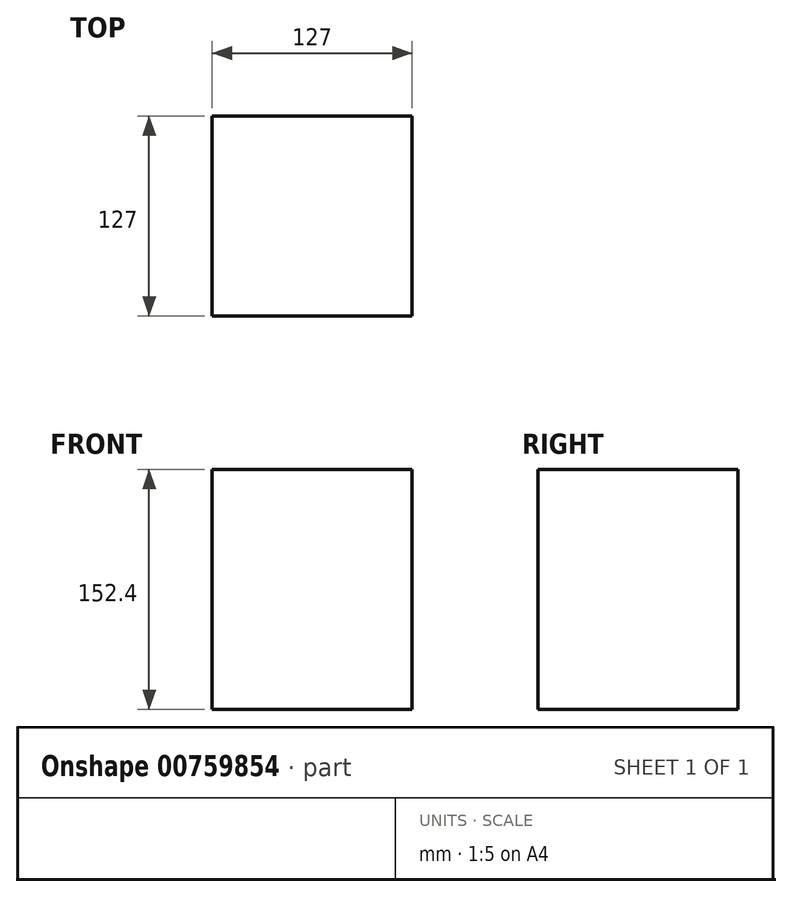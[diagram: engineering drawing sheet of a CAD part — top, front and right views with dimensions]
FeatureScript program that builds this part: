
annotation { "Feature Type Name" : "Feature", "Feature Type Description" : "" }
export const myFeature = defineFeature(function(context is Context, id is Id, definition is map)
    precondition{}
    {
        {
            var Q0;
            Q0=qCreatedBy(makeId("Top.planeOp"),FACE);
            var sketch = newSketch(context, id + "F0", { "sketchPlane" : qUnion([Q0])});
            skLineSegment(sketch, "E0.bottom", {"start": v(-62.5, 63.98) * mm, "end": v(64.5, 63.98) * mm});
            skLineSegment(sketch, "E0.top", {"start": v(-62.5, -63.02) * mm, "end": v(64.5, -63.02) * mm});
            skLineSegment(sketch, "E0.left", {"start": v(-62.5, 63.98) * mm, "end": v(-62.5, -63.02) * mm});
            skLineSegment(sketch, "E0.right", {"start": v(64.5, 63.98) * mm, "end": v(64.5, -63.02) * mm});
            skSolve(sketch);
        }
        {
            var Q0;
            Q0=makeQuery(id+"F0.imprint","IMPRINT",FACE,{"disambiguationData":[TD([[makeQuery(id+"F0.imprint","IMPRINT",EDGE,{"derivedFrom":sQuery(id+"F0.wireOp",EDGE,"E0.bottom")}),-1.0]])]});
            extrude(context, id + "F1", {"entities" : qUnion([Q0]), "depth" : 152.4 * mm, "offsetDistance" : 25.4 * mm});
        }
    });
